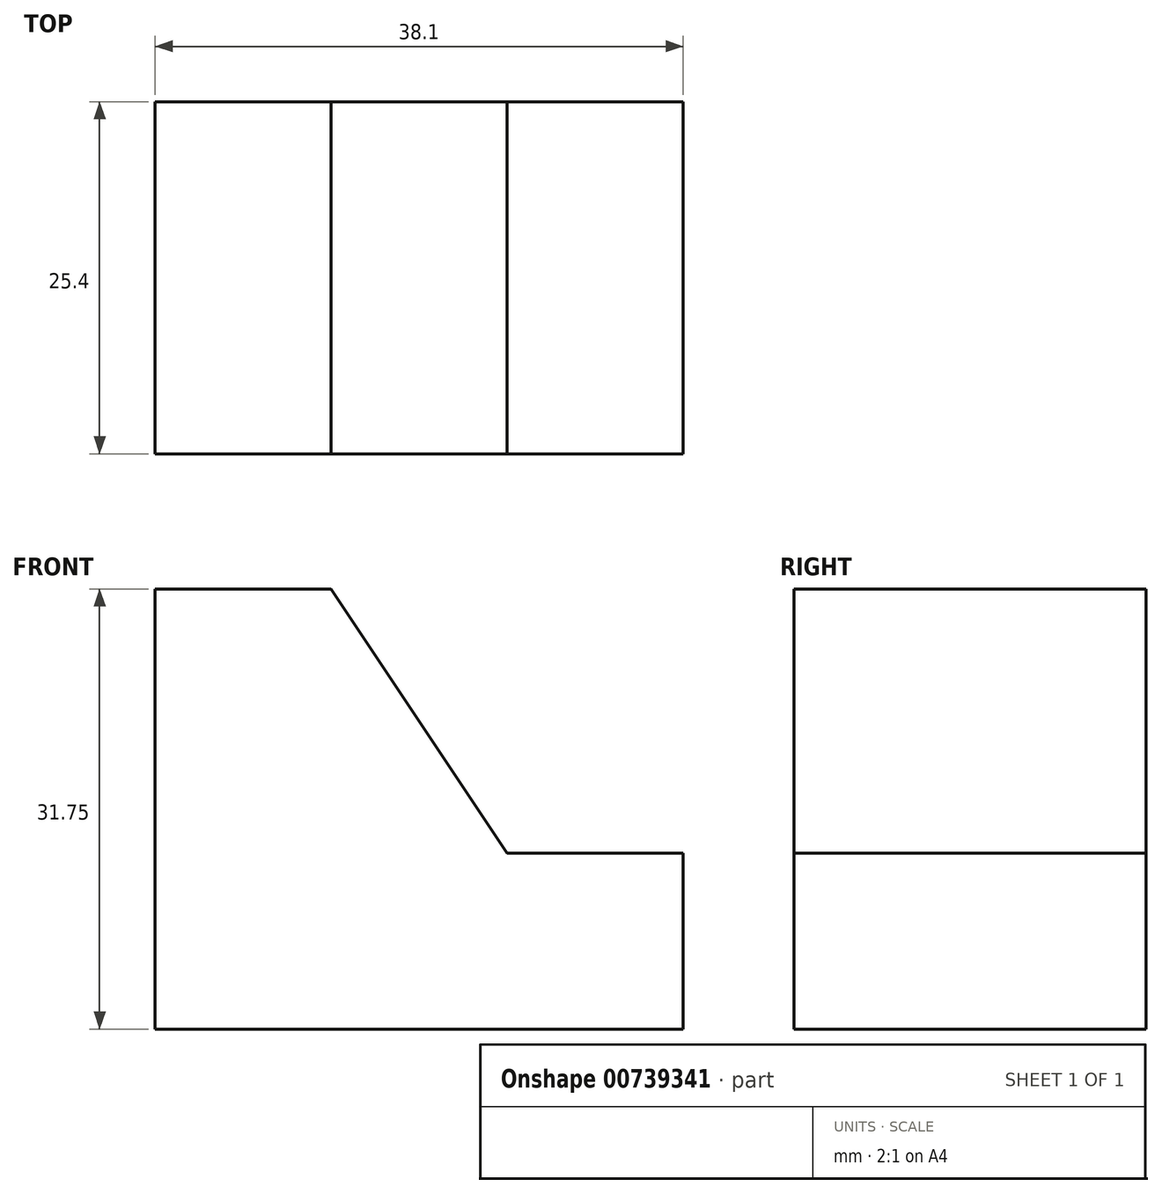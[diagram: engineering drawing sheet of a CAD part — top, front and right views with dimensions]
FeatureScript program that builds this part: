
annotation { "Feature Type Name" : "Feature", "Feature Type Description" : "" }
export const myFeature = defineFeature(function(context is Context, id is Id, definition is map)
    precondition{}
    {
        {
            var Q0;
            Q0=qCreatedBy(makeId("Front.planeOp"),FACE);
            var sketch = newSketch(context, id + "F0", { "sketchPlane" : qUnion([Q0])});
            skLineSegment(sketch, "E0", {"start": v(0, 0) * mm, "end": v(0, 31.75) * mm});
            skLineSegment(sketch, "E1", {"start": v(0, 31.75) * mm, "end": v(38.1, 31.75) * mm});
            skLineSegment(sketch, "E2", {"start": v(38.1, 31.75) * mm, "end": v(38.1, 0) * mm});
            skLineSegment(sketch, "E3", {"start": v(38.1, 0) * mm, "end": v(0, 0) * mm});
            skSolve(sketch);
        }
        {
            var Q0;
            Q0 = qSketchRegion(id + "F0", true);
            extrude(context, id + "F1", {"entities" : qUnion([Q0]), "depth" : 25.4 * mm, "offsetDistance" : 25.4 * mm});
        }
        {
            var Q0;
            Q0=makeQuery(id+"F1.opExtrude","CAP_FACE",FACE,{"disambiguationData":[OSD([sQuery(id+"F0.wireOp",EDGE,"E0"),sQuery(id+"F0.wireOp",EDGE,"E1"),sQuery(id+"F0.wireOp",EDGE,"E2"),sQuery(id+"F0.wireOp",EDGE,"E3")])],"isStart":false});
            var sketch = newSketch(context, id + "F2", { "sketchPlane" : qUnion([Q0])});
            skLineSegment(sketch, "E4", {"start": v(12.7, 31.75) * mm, "end": v(25.4, 12.7) * mm});
            skLineSegment(sketch, "E5", {"start": v(25.4, 12.7) * mm, "end": v(38.1, 12.7) * mm});
            skSolve(sketch);
        }
        {
            var Q0;
            Q0 = qSketchRegion(id + "F2", true);
            var Q1;
            {var subQ0=sQuery(id+"F2.wireOp",EDGE,"E4");Q1=makeQuery(id+"F2.imprint","IMPRINT",FACE,{"disambiguationData":[TD([[makeQuery(id+"F2.imprint","IMPRINT",EDGE,{"derivedFrom":subQ0}),1.0]])]});}
            extrude(context, id + "F3", {"entities" : qUnion([Q0, Q1]), "operationType" : NewBodyOperationType.REMOVE, "oppositeDirection" : true, "depth" : 25.4 * mm, "offsetDistance" : 25.4 * mm});
        }
    });
